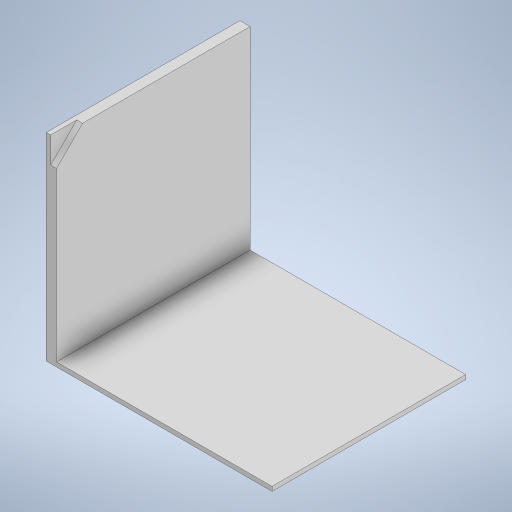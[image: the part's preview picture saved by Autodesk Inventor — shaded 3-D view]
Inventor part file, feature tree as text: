
AUTODESK INVENTOR PART (.ipt)
format: ipt  version: 2024 (Build 280153000, 153)  size: 321,536 bytes
history: native  units: mm
features: extrude x11, sketch x11
ambient origin geometry x8: Origin, YZ Plane, XZ Plane, XY Plane, X Axis, Y Axis, Z Axis, Center Point
bodies: Solid1 (feature_tree)
feature tree (22):
  extrude  "Top"  Depth=160.0mm
  extrude  "Right"  Depth=179.5mm
  extrude  "Left"  Depth=215.9mm
  extrude  "Plexiglass Cut"  Depth=25.4mm
  extrude  "Bottom"  Depth=266.7mm TaperAngle=0.0deg
  extrude  "Top Flattening"  Depth=266.7mm TaperAngle=0.0deg
  extrude  "Outer Side Flattening"  Depth=304.8mm TaperAngle=0.0deg
  extrude  "Bottom Flattening"  Depth=22.4mm TaperAngle=0.0deg
  extrude  "Inner Flattening"  Depth=22.389425mm
  extrude  "Top Cut"  Depth=22.4mm TaperAngle=0.0deg
  extrude  "Quarter Cut"  Depth=22.4mm TaperAngle=0.0deg
  sketch  "Sketch1"  dims[d11=220.0mm d12=160.0mm]
  sketch  "Sketch3"  dims[d15=248.6mm d16=179.5mm]
  sketch  "Sketch4"  dims[d18=304.8mm d19=215.9mm]
  sketch  "Sketch5"  dims[d20=25.4mm d21=0.0mm d22=25.4mm]
  sketch  "Sketch6"  dims[d25=266.7mm d26=50.8mm d27=0.0mm]
  sketch  "Sketch9"  dims[d28=266.7mm d29=50.8mm d30=0.0mm]
  sketch  "Sketch10"  dims[d31=12.7mm d32=304.8mm d33=0.0mm]
  sketch  "Sketch11"  dims[d34=25.4mm d35=0.0mm d46=22.4mm d47=0.0mm]
  sketch  "Sketch12"  dims[d48=22.389425mm d49=22.389425mm]
  sketch  "Sketch13"  dims[d50=0.0mm d51=0.0mm d52=22.4mm d53=0.0mm]
  sketch  "Sketch14"  dims[d54=296.8mm d55=22.4mm d56=0.0mm d57=0.0mm d58=0.0mm d59=0.0mm d60=0.0mm]
